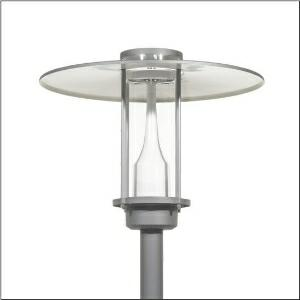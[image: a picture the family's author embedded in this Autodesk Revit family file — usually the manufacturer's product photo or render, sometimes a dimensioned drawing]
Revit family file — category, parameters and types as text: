
# Revit family: city-light_plus_iq___st1_2a_5xa5275af14hp_3410
name_source: partatom
category: Lighting Fixtures
units: mm (PartAtom-declared; Revit-internal decimal feet)

## family parameters
Cut with Voids When Loaded = No
Host = Face
Light Source = No
Part Type = Normal
Room Calculation Point = No
Round Connector Dimension = Use Diameter
Shared = No

## types (1)
- --- (1 x LED, 3730 lm, 33.6 W, 2200K)
    Apparent Load = 34 VA
    CIE Flux Codes = 22 60 93 97 100
    Color Rendering = 70
    Color Temperature = 2200K
    Default Elevation = 1800 mm
    Description = City-Light Plus iQ, mast luminaire, Module 540 iQ-SR, primary light control with 3 zone facetted reflector, of plastic, silver coated, highly specular, structured, primary optical cover: cover, of PMMA, transparent, light distribution: ST1.2a, light emission: direct distribution, primary light characteristic: asymmetric, installation type: post-top, LED, High Power LED, rated luminous flux: 3.730lm, luminous efficacy: 111lm/W, light colour: 722, colour temperature: 2200K, control gear: iQ Street-Remote, control: pre-setting: logarithmic dimming characteristic, Street-Remote, Auto-Match, Temp-Guard, Lumen-Switch, Night-Set, Smart-Wire, Light-Fading, Desk-Remote (wireless, voltage-free reading and setting of iQ features in the workshop via application-optimized NFC function/RFID function), optimised constant luminous flux control (CLO 2.0), with terminal, 6-pole, max. 2.5mm², mains connection: 230..240V, AC, 50/60Hz, start of lifetime: 34W, end of service life: 36W, reduction: 15W, luminaire housing, upper part, of glass-fibre reinforced polyester, coated, Siteco® metallic grey (DB 702S), diameter: 750mm, height: 590mm, spigot size: d x l = 76 x 70mm (post-top) | with reducer (optional accessory) 60 x 70mm, mounting height: 3..5m, post-top mast mounting element, of diecast aluminium, coated, Siteco® metallic grey (DB 702S), Module 540 iQ-SR, traffic white (RAL 9016), equipment: Power, protection rating (complete): IP65, insulation class (complete): insulation class II (safety insulation), certification: CE, ENEC, VDE, packaging unit: 1 piece

Light Distribution: ST1.2a
    Height = 590 mm
    Lamp = 1 x LED
    Lamp Light Flux = 3730 lm
    Lamp Power = 33.6 W
    Lamp count = 1
    Length = 750 mm
    Luminous efficacy = 111 lm/W
    Manufacturer = Siteco
    ModVariant = No
    Model = 5XA5275AF14HP
    Number of Poles = 1
    OnlyDefault = Yes
    Power Factor = 1
    Product Name = City-Light Plus iQ | ST1.2a
    Product group = mast luminaire | pylon top
    ProductGroupID = 6100
    Protection Class = Protection class II
    Protection Degree = IP 65
    RLX_Detail_Level = 1
    RLX_Emergency_Light_Flux = 0 lm
    RLX_Emergency_Type = 0
    RLX_Emergency_Type_DB = No
    RlxData = <blob elided: 52633 chars, md5=506c6e5c>
    Socket = socket
    Standby Power = 0 W
    System Light Flux = 3730 lm
    System Power = 34 W
    Type Comments = factory setting: luminous flux: 100 % | dim-lin: 254 | 695 mA
    Type Image = l_1006456.jpg
    URL = http://relux.com
    VarID = @adj_191351
    Voltage = 0 V
    Weight = 0.00 kg
    Width = 0 mm  [stored 0 ft]

note: [stored X ft] marks values corroborated as IEEE doubles in the binary element streams (Revit-internal decimal feet)

## geometry (parser evidence)
native form markers: Blend x4, Sweep x9
no freeform markers — native parametric forms only
